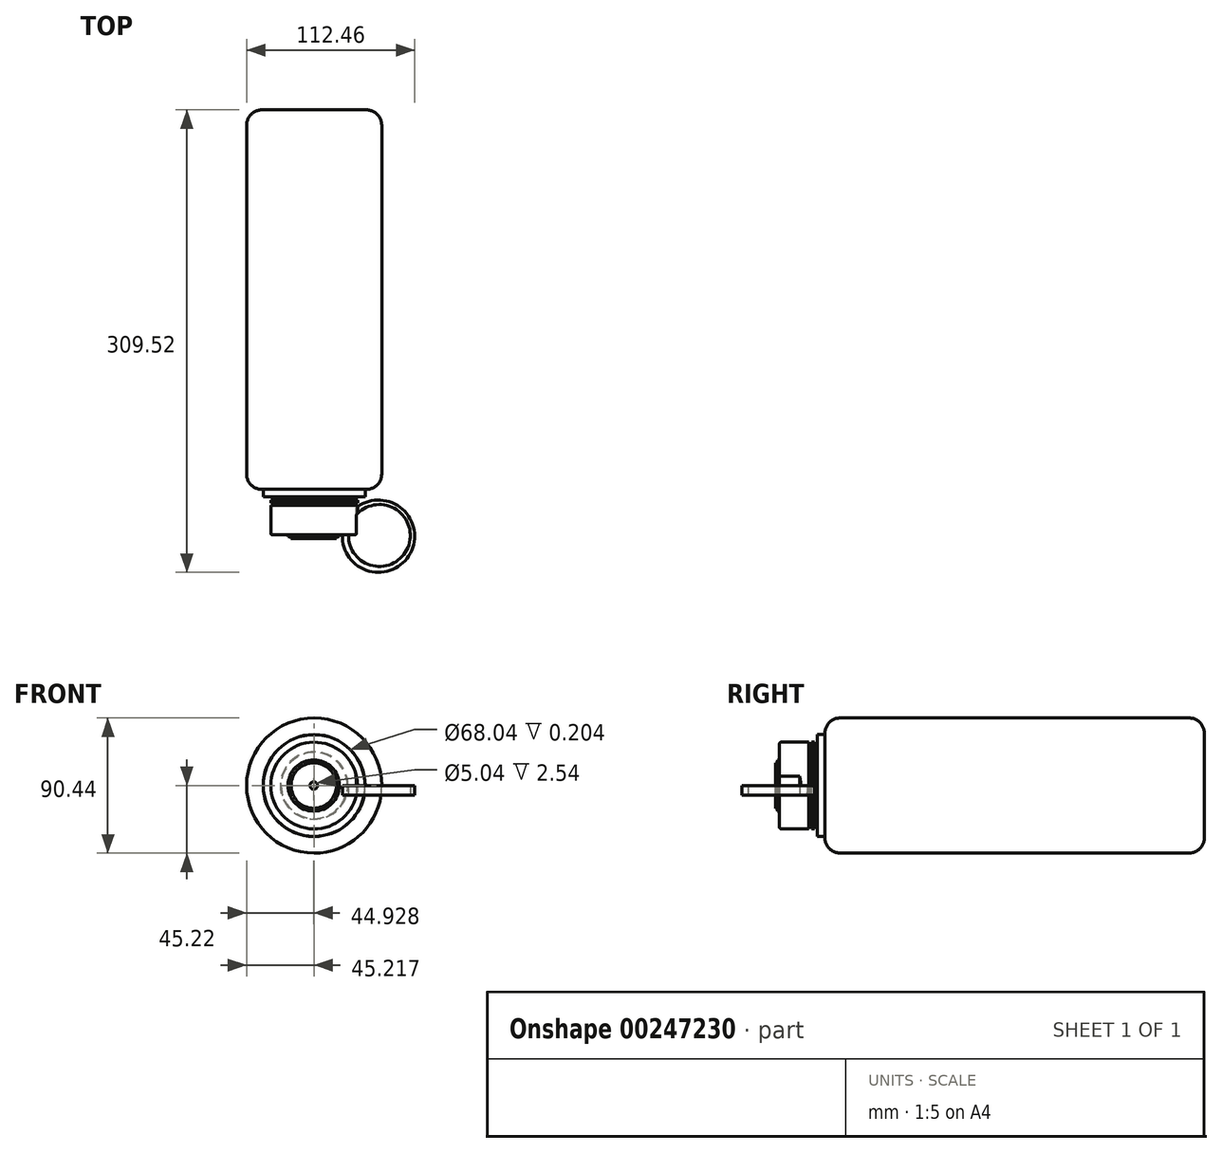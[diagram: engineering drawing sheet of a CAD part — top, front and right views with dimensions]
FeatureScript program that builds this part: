
annotation { "Feature Type Name" : "Feature", "Feature Type Description" : "" }
export const myFeature = defineFeature(function(context is Context, id is Id, definition is map)
    precondition{}
    {
        {
            var Q0;
            Q0=qCreatedBy(makeId("Front.planeOp"),FACE);
            var sketch = newSketch(context, id + "F0", { "sketchPlane" : qUnion([Q0])});
            skCircle(sketch, "E0", {"center": v(-2.88, 0) * mm, "radius": 45.22 * mm});
            skSolve(sketch);
        }
        {
            var Q0;
            Q0 = qSketchRegion(id + "F0", true);
            extrude(context, id + "F1", {"entities" : qUnion([Q0]), "depth" : 254 * mm});
        }
        {
            var Q0;
            Q0=makeQuery(id+"F1.opExtrude","CAP_FACE",FACE,{"disambiguationData":[OSD([sQuery(id+"F0.wireOp",EDGE,"E0")])],"isStart":false});
            fillet(context, id + "F2", {"entities" : qUnion([Q0]), "radius" : 10.16 * mm, "tangentPropagation" : true, "allowEdgeOverflow" : false});
        }
        {
            var Q0;
            Q0=makeQuery(id+"F1.opExtrude","CAP_FACE",FACE,{"disambiguationData":[OSD([sQuery(id+"F0.wireOp",EDGE,"E0")])],"isStart":true});
            fillet(context, id + "F3", {"entities" : qUnion([Q0]), "radius" : 10.16 * mm, "tangentPropagation" : true, "allowEdgeOverflow" : false});
        }
        {
            var Q0;
            Q0=makeQuery(id+"F1.opExtrude","CAP_FACE",FACE,{"disambiguationData":[OSD([sQuery(id+"F0.wireOp",EDGE,"E0")])],"isStart":false});
            var sketch = newSketch(context, id + "F4", { "sketchPlane" : qUnion([Q0])});
            skPoint(sketch, "E1", {"position": v(-2.88, 0) * mm});
            skCircle(sketch, "E2", {"center": v(-2.88, 0) * mm, "radius": 34.12 * mm});
            skSolve(sketch);
        }
        {
            var Q0;
            Q0 = qSketchRegion(id + "F4", true);
            extrude(context, id + "F5", {"entities" : qUnion([Q0]), "depth" : 5.08 * mm});
        }
        {
            var Q0;
            Q0 = qSketchRegion(id + "F4", true);
            extrude(context, id + "F6", {"entities" : qUnion([Q0]), "depth" : 5.08 * mm});
        }
        {
            var Q0;
            Q0=makeQuery(id+"F5.opExtrude","CAP_FACE",FACE,{"disambiguationData":[OSD([sQuery(id+"F4.wireOp",EDGE,"E2")])],"isStart":false});
            var sketch = newSketch(context, id + "F7", { "sketchPlane" : qUnion([Q0])});
            skPoint(sketch, "E3", {"position": v(-2.88, 0) * mm});
            skCircle(sketch, "E4", {"center": v(-2.88, 0) * mm, "radius": 29.03 * mm});
            skLineSegment(sketch, "E5", {"start": v(-2.88, -29.03) * mm, "end": v(-2.88, 29.03) * mm, "construction": true});
            skSolve(sketch);
        }
        {
            var Q0;
            Q0 = qSketchRegion(id + "F7", true);
            extrude(context, id + "F8", {"entities" : qUnion([Q0]), "operationType" : NewBodyOperationType.ADD, "depth" : 25.4 * mm});
        }
        {
            var Q0;
            Q0=makeQuery(id+"F8.opExtrude","CAP_FACE",FACE,{"disambiguationData":[OSD([sQuery(id+"F7.wireOp",EDGE,"E4")])],"isStart":false});
            fillet(context, id + "F9", {"entities" : qUnion([Q0]), "radius" : 1.27 * mm, "tangentPropagation" : true, "allowEdgeOverflow" : false});
        }
        {
            var Q0;
            Q0=makeQuery(id+"F8.opExtrude","CAP_FACE",FACE,{"disambiguationData":[OSD([sQuery(id+"F7.wireOp",EDGE,"E4")])],"isStart":false});
            var sketch = newSketch(context, id + "F10", { "sketchPlane" : qUnion([Q0])});
            skPoint(sketch, "E6", {"position": v(-2.88, 0) * mm});
            skLineSegment(sketch, "E7", {"start": v(-2.88, 27.76) * mm, "end": v(-2.88, -27.76) * mm, "construction": true});
            skSolve(sketch);
        }
        {
            var Q0;
            Q0=sQuery(id+"F10.wireOp",EDGE,"E7");
            var Q1;
            {var subQ0=sQuery(id+"F7.wireOp",EDGE,"E4");Q1=makeQuery(id+"F9.opFillet","BLEND_EDGE",EDGE,{"blendedFrom":[makeQuery(id+"F8.opExtrude","CAP_EDGE",EDGE,{"disambiguationData":[OSD([subQ0])],"isStart":false}),makeQuery(id+"F8.opExtrude","CAP_FACE",FACE,{"disambiguationData":[OSD([subQ0])],"isStart":false})],"blendedInto":[makeQuery(id+"F8.opExtrude","CAP_FACE",FACE,{"disambiguationData":[OSD([subQ0])],"isStart":false})]});}
            cPlane(context, id + "F11", {"entities" : qUnion([Q0, Q1]), "cplaneType" : CPlaneType.LINE_ANGLE, "offset" : 25.4 * mm, "angle" : 180 * degree, "width" : 152.4 * mm, "height" : 152.4 * mm});
        }
        {
            var Q0;
            Q0=qCreatedBy(id+"F11.planeOp",FACE);
            var sketch = newSketch(context, id + "F12", { "sketchPlane" : qUnion([Q0])});
            skLineSegment(sketch, "E8.bottom", {"start": v(-258.88, -22.59) * mm, "end": v(-261.05, -22.59) * mm});
            skLineSegment(sketch, "E8.top", {"start": v(-258.88, -34.02) * mm, "end": v(-261.05, -34.02) * mm});
            skLineSegment(sketch, "E8.left", {"start": v(-258.88, -22.59) * mm, "end": v(-258.88, -34.02) * mm});
            skLineSegment(sketch, "E8.right", {"start": v(-261.05, -22.59) * mm, "end": v(-261.05, -34.02) * mm});
            skSolve(sketch);
        }
        {
            var Q0;
            Q0 = qSketchRegion(id + "F12", true);
            var Q1;
            {var subQ0=sQuery(id+"F7.wireOp",EDGE,"E4");Q1=makeQuery(id+"F9.opFillet","BLEND_EDGE",EDGE,{"blendedFrom":[makeQuery(id+"F8.opExtrude","CAP_EDGE",EDGE,{"disambiguationData":[OSD([subQ0])],"isStart":false}),makeQuery(id+"F8.opExtrude","CAP_FACE",FACE,{"disambiguationData":[OSD([subQ0])],"isStart":false})],"blendedInto":[makeQuery(id+"F8.opExtrude","CAP_FACE",FACE,{"disambiguationData":[OSD([subQ0])],"isStart":false})]});}
            revolve(context, id + "F13", {"operationType" : NewBodyOperationType.REMOVE, "entities" : qUnion([Q0]), "axis" : qUnion([Q1]), "revolveType" : RevolveType.FULL, "oppositeDirection" : true});
        }
        {
            var Q0;
            Q0=qCreatedBy(id+"F11.planeOp",FACE);
            var sketch = newSketch(context, id + "F14", { "sketchPlane" : qUnion([Q0])});
            skLineSegment(sketch, "E9.bottom", {"start": v(-264.74, -22.16) * mm, "end": v(-263.05, -22.16) * mm});
            skLineSegment(sketch, "E9.top", {"start": v(-264.74, -31.03) * mm, "end": v(-263.05, -31.03) * mm});
            skLineSegment(sketch, "E9.left", {"start": v(-264.74, -22.16) * mm, "end": v(-264.74, -31.03) * mm});
            skLineSegment(sketch, "E9.right", {"start": v(-263.05, -22.16) * mm, "end": v(-263.05, -31.03) * mm});
            skSolve(sketch);
        }
        {
            var Q0;
            Q0 = qSketchRegion(id + "F14", true);
            var Q1;
            {var subQ0=sQuery(id+"F7.wireOp",EDGE,"E4");Q1=makeQuery(id+"F9.opFillet","BLEND_EDGE",EDGE,{"blendedFrom":[makeQuery(id+"F8.opExtrude","CAP_EDGE",EDGE,{"disambiguationData":[OSD([subQ0])],"isStart":false}),makeQuery(id+"F8.opExtrude","CAP_FACE",FACE,{"disambiguationData":[OSD([subQ0])],"isStart":false})],"blendedInto":[makeQuery(id+"F8.opExtrude","CAP_FACE",FACE,{"disambiguationData":[OSD([subQ0])],"isStart":false})]});}
            revolve(context, id + "F15", {"operationType" : NewBodyOperationType.REMOVE, "entities" : qUnion([Q0]), "axis" : qUnion([Q1]), "revolveType" : RevolveType.FULL, "oppositeDirection" : true});
        }
        {
            var Q0;
            {var subQ0=sQuery(id+"F7.wireOp",EDGE,"E4");Q0=makeQuery(id+"F10.imprint","IMPRINT",FACE,{"disambiguationData":[TD([[makeQuery(id+"F10.imprint","IMPRINT",EDGE,{"derivedFrom":makeQuery(id+"F9.opFillet","BLEND_EDGE",EDGE,{"blendedFrom":[makeQuery(id+"F8.opExtrude","CAP_EDGE",EDGE,{"disambiguationData":[OSD([subQ0])],"isStart":false}),makeQuery(id+"F8.opExtrude","CAP_FACE",FACE,{"disambiguationData":[OSD([subQ0])],"isStart":false})],"blendedInto":[makeQuery(id+"F8.opExtrude","CAP_FACE",FACE,{"disambiguationData":[OSD([subQ0])],"isStart":false})]})}),1.0]])]});}
            var sketch = newSketch(context, id + "F16", { "sketchPlane" : qUnion([Q0])});
            skCircle(sketch, "E10", {"center": v(-3.17, 0) * mm, "radius": 17.16 * mm});
            skSolve(sketch);
        }
        {
            var Q0;
            Q0 = qSketchRegion(id + "F16", true);
            extrude(context, id + "F17", {"entities" : qUnion([Q0]), "operationType" : NewBodyOperationType.ADD, "depth" : 1.27 * mm});
        }
        {
            var Q0;
            Q0=makeQuery(id+"F17.opExtrude","CAP_FACE",FACE,{"disambiguationData":[OSD([sQuery(id+"F16.wireOp",EDGE,"E10")])],"isStart":false});
            var sketch = newSketch(context, id + "F18", { "sketchPlane" : qUnion([Q0])});
            skCircle(sketch, "E11", {"center": v(-3.17, 0) * mm, "radius": 15.18 * mm});
            skSolve(sketch);
        }
        {
            var Q0;
            Q0 = qSketchRegion(id + "F18", true);
            extrude(context, id + "F19", {"entities" : qUnion([Q0]), "operationType" : NewBodyOperationType.ADD, "depth" : 1.27 * mm});
        }
        {
            var Q0;
            Q0=makeQuery(id+"F19.opExtrude","CAP_FACE",FACE,{"disambiguationData":[OSD([sQuery(id+"F18.wireOp",EDGE,"E11")])],"isStart":false});
            var sketch = newSketch(context, id + "F20", { "sketchPlane" : qUnion([Q0])});
            skCircle(sketch, "E12", {"center": v(-3.17, 0) * mm, "radius": 2.52 * mm});
            skSolve(sketch);
        }
        {
            var Q0;
            Q0 = qSketchRegion(id + "F20", true);
            extrude(context, id + "F21", {"entities" : qUnion([Q0]), "operationType" : NewBodyOperationType.REMOVE, "oppositeDirection" : true, "depth" : 2.54 * mm});
        }
        {
            var Q0;
            Q0=makeQuery(id+"F19.opExtrude","CAP_FACE",FACE,{"disambiguationData":[OSD([sQuery(id+"F18.wireOp",EDGE,"E11")])],"isStart":false});
            var sketch = newSketch(context, id + "F22", { "sketchPlane" : qUnion([Q0])});
            skLineSegment(sketch, "E13", {"start": v(0, 0) * mm, "end": v(39.9, 0) * mm, "construction": true});
            skSolve(sketch);
        }
        {
            var Q0;
            Q0=sQuery(id+"F22.wireOp",EDGE,"E13");
            cPlane(context, id + "F23", {"entities" : qUnion([Q0]), "cplaneType" : CPlaneType.LINE_ANGLE, "offset" : 25.4 * mm, "angle" : 90 * degree, "width" : 152.4 * mm, "height" : 152.4 * mm});
        }
        {
            var Q0;
            Q0=qCreatedBy(id+"F23.planeOp",FACE);
            var sketch = newSketch(context, id + "F24", { "sketchPlane" : qUnion([Q0])});
            skCircle(sketch, "E14", {"center": v(40.18, -285.34) * mm, "radius": 24.18 * mm});
            skSolve(sketch);
        }
        {
            var Q0;
            Q0 = qSketchRegion(id + "F24", true);
            extrude(context, id + "F25", {"entities" : qUnion([Q0]), "operationType" : NewBodyOperationType.ADD, "oppositeDirection" : true, "depth" : 6.35 * mm});
        }
        {
            var Q0;
            Q0=makeQuery(id+"F25.opExtrude","CAP_FACE",FACE,{"disambiguationData":[OSD([sQuery(id+"F24.wireOp",EDGE,"E14")])],"isStart":false});
            var sketch = newSketch(context, id + "F26", { "sketchPlane" : qUnion([Q0])});
            skArc(sketch, "E15", {"start": v(25.44, 270.95) * mm, "mid": v(60.03, 292.49) * mm, "end": v(20.08, 284.48) * mm});
            skSolve(sketch);
        }
        {
            var Q0;
            {var subQ0=sQuery(id+"F26.wireOp",EDGE,"E15");Q0=makeQuery(id+"F26.imprint","IMPRINT",FACE,{"disambiguationData":[TD([[makeQuery(id+"F26.imprint","IMPRINT",EDGE,{"derivedFrom":subQ0}),1.0]])]});}
            var Q1;
            Q1=sQuery(id+"F26.wireOp",EDGE,"E15");
            extrude(context, id + "F27", {"entities" : qUnion([Q0]), "operationType" : NewBodyOperationType.REMOVE, "surfaceEntities" : qUnion([Q1]), "oppositeDirection" : true, "depth" : 25.4 * mm});
        }
    });
